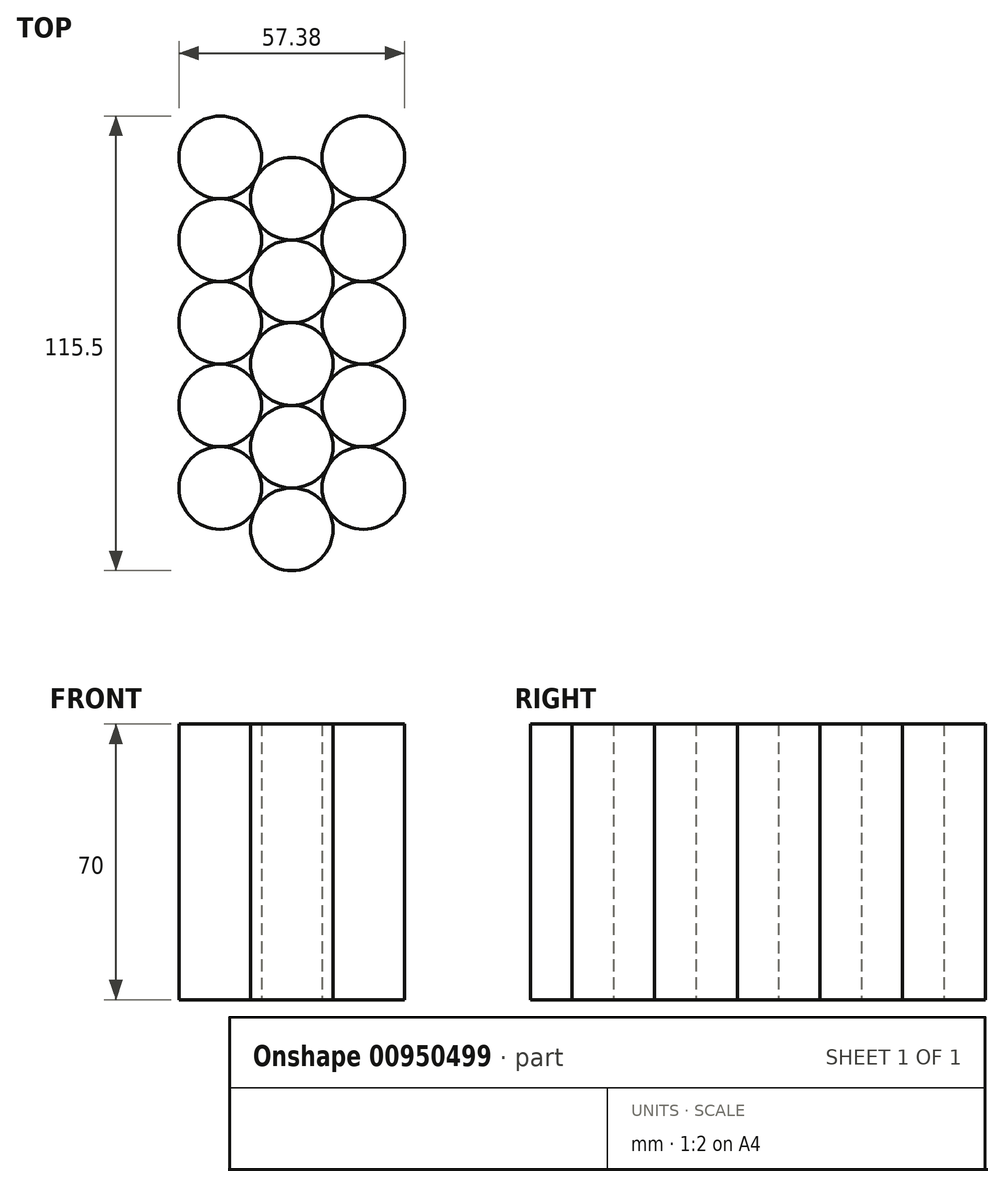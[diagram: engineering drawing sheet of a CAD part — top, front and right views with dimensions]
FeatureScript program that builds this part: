
annotation { "Feature Type Name" : "Feature", "Feature Type Description" : "" }
export const myFeature = defineFeature(function(context is Context, id is Id, definition is map)
    precondition{}
    {
        {
            var Q0;
            Q0=qCreatedBy(makeId("Top.planeOp"),FACE);
            var sketch = newSketch(context, id + "F0", { "sketchPlane" : qUnion([Q0])});
            skCircle(sketch, "E0", {"center": v(0, 0) * mm, "radius": 10.5 * mm});
            skCircle(sketch, "E1.0.1.0", {"center": v(0, 21) * mm, "radius": 10.5 * mm});
            skCircle(sketch, "E1.0.2.0", {"center": v(0, 42) * mm, "radius": 10.5 * mm});
            skCircle(sketch, "E1.0.3.0", {"center": v(0, 63) * mm, "radius": 10.5 * mm});
            skLineSegment(sketch, "E1.direction1", {"start": v(0, 0) * mm, "end": v(25, 0) * mm, "construction": true});
            skLineSegment(sketch, "E1.direction2", {"start": v(0, 0) * mm, "end": v(0, 21) * mm, "construction": true});
            skCircle(sketch, "E2", {"center": v(18.19, 10.5) * mm, "radius": 10.5 * mm});
            skCircle(sketch, "E3.0.1.0", {"center": v(18.19, 31.5) * mm, "radius": 10.5 * mm});
            skCircle(sketch, "E3.0.2.0", {"center": v(18.19, 52.5) * mm, "radius": 10.5 * mm});
            skCircle(sketch, "E3.0.3.0", {"center": v(18.19, 73.5) * mm, "radius": 10.5 * mm});
            skLineSegment(sketch, "E3.direction1", {"start": v(18.19, 10.5) * mm, "end": v(43.19, 10.5) * mm, "construction": true});
            skLineSegment(sketch, "E3.direction2", {"start": v(18.19, 10.5) * mm, "end": v(18.19, 31.5) * mm, "construction": true});
            skCircle(sketch, "E4", {"center": v(-18.19, 10.5) * mm, "radius": 10.5 * mm});
            skCircle(sketch, "E5.0.1.0", {"center": v(-18.19, 31.5) * mm, "radius": 10.5 * mm});
            skCircle(sketch, "E5.0.2.0", {"center": v(-18.19, 52.5) * mm, "radius": 10.5 * mm});
            skCircle(sketch, "E5.0.3.0", {"center": v(-18.19, 73.5) * mm, "radius": 10.5 * mm});
            skLineSegment(sketch, "E5.direction1", {"start": v(-18.19, 10.5) * mm, "end": v(9.41, 10.5) * mm, "construction": true});
            skLineSegment(sketch, "E5.direction2", {"start": v(-18.19, 10.5) * mm, "end": v(-18.19, 31.5) * mm, "construction": true});
            skLineSegment(sketch, "E6", {"start": v(0, -10.5) * mm, "end": v(0, 94.5) * mm, "construction": true});
            skCircle(sketch, "E7.0.0.4", {"center": v(0, 84) * mm, "radius": 10.5 * mm});
            skCircle(sketch, "E8", {"center": v(-18.19, 94.5) * mm, "radius": 10.5 * mm});
            skCircle(sketch, "E9", {"center": v(18.19, 94.5) * mm, "radius": 10.5 * mm});
            skSolve(sketch);
        }
        {
            var Q0;
            {var subQ0=sQuery(id+"F0.wireOp",EDGE,"E0");var subQ1=makeQuery(id+"F0.imprint","INTERSECT",VERTEX,{"derivedFrom":[subQ0,sQuery(id+"F0.wireOp",EDGE,"E1.0.1.0")]});Q0=makeQuery(id+"F0.imprint","IMPRINT",FACE,{"disambiguationData":[TD([[makeQuery(id+"F0.imprint","IMPRINT",EDGE,{"disambiguationData":[TD([[subQ1,1.0]])],"derivedFrom":subQ0}),1.0]])]});}
            var Q1;
            {var subQ0=sQuery(id+"F0.wireOp",EDGE,"E2");var subQ1=makeQuery(id+"F0.imprint","INTERSECT",VERTEX,{"derivedFrom":[subQ0,sQuery(id+"F0.wireOp",EDGE,"E3.0.1.0")]});Q1=makeQuery(id+"F0.imprint","IMPRINT",FACE,{"disambiguationData":[TD([[makeQuery(id+"F0.imprint","IMPRINT",EDGE,{"disambiguationData":[TD([[subQ1,-1.0]])],"derivedFrom":subQ0}),1.0]])]});}
            var Q2;
            {var subQ0=sQuery(id+"F0.wireOp",EDGE,"E1.0.1.0");var subQ1=makeQuery(id+"F0.imprint","INTERSECT",VERTEX,{"derivedFrom":[subQ0,sQuery(id+"F0.wireOp",EDGE,"E1.0.2.0")]});Q2=makeQuery(id+"F0.imprint","IMPRINT",FACE,{"disambiguationData":[TD([[makeQuery(id+"F0.imprint","IMPRINT",EDGE,{"disambiguationData":[TD([[subQ1,1.0]])],"derivedFrom":subQ0}),1.0]])]});}
            var Q3;
            {var subQ0=sQuery(id+"F0.wireOp",EDGE,"E3.0.1.0");var subQ1=makeQuery(id+"F0.imprint","INTERSECT",VERTEX,{"derivedFrom":[subQ0,sQuery(id+"F0.wireOp",EDGE,"E3.0.2.0")]});Q3=makeQuery(id+"F0.imprint","IMPRINT",FACE,{"disambiguationData":[TD([[makeQuery(id+"F0.imprint","IMPRINT",EDGE,{"disambiguationData":[TD([[subQ1,-1.0]])],"derivedFrom":subQ0}),1.0]])]});}
            var Q4;
            {var subQ0=sQuery(id+"F0.wireOp",EDGE,"E1.0.2.0");var subQ1=makeQuery(id+"F0.imprint","INTERSECT",VERTEX,{"derivedFrom":[subQ0,sQuery(id+"F0.wireOp",EDGE,"E1.0.3.0")]});Q4=makeQuery(id+"F0.imprint","IMPRINT",FACE,{"disambiguationData":[TD([[makeQuery(id+"F0.imprint","IMPRINT",EDGE,{"disambiguationData":[TD([[subQ1,1.0]])],"derivedFrom":subQ0}),1.0]])]});}
            var Q5;
            {var subQ0=sQuery(id+"F0.wireOp",EDGE,"E3.0.2.0");var subQ1=makeQuery(id+"F0.imprint","INTERSECT",VERTEX,{"derivedFrom":[subQ0,sQuery(id+"F0.wireOp",EDGE,"E3.0.3.0")]});Q5=makeQuery(id+"F0.imprint","IMPRINT",FACE,{"disambiguationData":[TD([[makeQuery(id+"F0.imprint","IMPRINT",EDGE,{"disambiguationData":[TD([[subQ1,-1.0]])],"derivedFrom":subQ0}),1.0]])]});}
            var Q6;
            {var subQ0=sQuery(id+"F0.wireOp",EDGE,"E1.0.3.0");var subQ1=makeQuery(id+"F0.imprint","INTERSECT",VERTEX,{"derivedFrom":[subQ0,sQuery(id+"F0.wireOp",EDGE,"E1.0.4.0")]});Q6=makeQuery(id+"F0.imprint","IMPRINT",FACE,{"disambiguationData":[TD([[makeQuery(id+"F0.imprint","IMPRINT",EDGE,{"disambiguationData":[TD([[subQ1,1.0]])],"derivedFrom":subQ0}),1.0]])]});}
            var Q7;
            {var subQ0=sQuery(id+"F0.wireOp",EDGE,"E3.0.3.0");var subQ1=makeQuery(id+"F0.imprint","INTERSECT",VERTEX,{"derivedFrom":[subQ0,sQuery(id+"F0.wireOp",EDGE,"E3.0.4.0")]});Q7=makeQuery(id+"F0.imprint","IMPRINT",FACE,{"disambiguationData":[TD([[makeQuery(id+"F0.imprint","IMPRINT",EDGE,{"disambiguationData":[TD([[subQ1,-1.0]])],"derivedFrom":subQ0}),1.0]])]});}
            var Q8;
            {var subQ0=sQuery(id+"F0.wireOp",EDGE,"E1.0.4.0");var subQ1=makeQuery(id+"F0.imprint","INTERSECT",VERTEX,{"derivedFrom":[subQ0,sQuery(id+"F0.wireOp",EDGE,"E1.0.5.0")]});Q8=makeQuery(id+"F0.imprint","IMPRINT",FACE,{"disambiguationData":[TD([[makeQuery(id+"F0.imprint","IMPRINT",EDGE,{"disambiguationData":[TD([[subQ1,1.0]])],"derivedFrom":subQ0}),1.0]])]});}
            var Q9;
            {var subQ0=sQuery(id+"F0.wireOp",EDGE,"E3.0.4.0");var subQ1=makeQuery(id+"F0.imprint","INTERSECT",VERTEX,{"derivedFrom":[subQ0,sQuery(id+"F0.wireOp",EDGE,"E3.0.5.0")]});Q9=makeQuery(id+"F0.imprint","IMPRINT",FACE,{"disambiguationData":[TD([[makeQuery(id+"F0.imprint","IMPRINT",EDGE,{"disambiguationData":[TD([[subQ1,-1.0]])],"derivedFrom":subQ0}),1.0]])]});}
            var Q10;
            {var subQ0=sQuery(id+"F0.wireOp",EDGE,"E1.0.5.0");var subQ1=makeQuery(id+"F0.imprint","INTERSECT",VERTEX,{"derivedFrom":[subQ0,sQuery(id+"F0.wireOp",EDGE,"E1.0.6.0")]});Q10=makeQuery(id+"F0.imprint","IMPRINT",FACE,{"disambiguationData":[TD([[makeQuery(id+"F0.imprint","IMPRINT",EDGE,{"disambiguationData":[TD([[subQ1,1.0]])],"derivedFrom":subQ0}),1.0]])]});}
            var Q11;
            {var subQ0=sQuery(id+"F0.wireOp",EDGE,"E3.0.5.0");var subQ1=makeQuery(id+"F0.imprint","INTERSECT",VERTEX,{"derivedFrom":[subQ0,sQuery(id+"F0.wireOp",EDGE,"E3.0.6.0")]});Q11=makeQuery(id+"F0.imprint","IMPRINT",FACE,{"disambiguationData":[TD([[makeQuery(id+"F0.imprint","IMPRINT",EDGE,{"disambiguationData":[TD([[subQ1,-1.0]])],"derivedFrom":subQ0}),1.0]])]});}
            var Q12;
            {var subQ0=sQuery(id+"F0.wireOp",EDGE,"E1.0.6.0");var subQ1=makeQuery(id+"F0.imprint","INTERSECT",VERTEX,{"derivedFrom":[subQ0,sQuery(id+"F0.wireOp",EDGE,"E1.0.7.0")]});Q12=makeQuery(id+"F0.imprint","IMPRINT",FACE,{"disambiguationData":[TD([[makeQuery(id+"F0.imprint","IMPRINT",EDGE,{"disambiguationData":[TD([[subQ1,1.0]])],"derivedFrom":subQ0}),1.0]])]});}
            var Q13;
            {var subQ0=sQuery(id+"F0.wireOp",EDGE,"E3.0.6.0");var subQ1=makeQuery(id+"F0.imprint","INTERSECT",VERTEX,{"derivedFrom":[subQ0,sQuery(id+"F0.wireOp",EDGE,"E3.0.7.0")]});Q13=makeQuery(id+"F0.imprint","IMPRINT",FACE,{"disambiguationData":[TD([[makeQuery(id+"F0.imprint","IMPRINT",EDGE,{"disambiguationData":[TD([[subQ1,-1.0]])],"derivedFrom":subQ0}),1.0]])]});}
            var Q14;
            {var subQ0=sQuery(id+"F0.wireOp",EDGE,"E1.0.7.0");var subQ1=makeQuery(id+"F0.imprint","INTERSECT",VERTEX,{"derivedFrom":[subQ0,sQuery(id+"F0.wireOp",EDGE,"E1.0.8.0")]});Q14=makeQuery(id+"F0.imprint","IMPRINT",FACE,{"disambiguationData":[TD([[makeQuery(id+"F0.imprint","IMPRINT",EDGE,{"disambiguationData":[TD([[subQ1,1.0]])],"derivedFrom":subQ0}),1.0]])]});}
            var Q15;
            {var subQ0=sQuery(id+"F0.wireOp",EDGE,"E3.0.7.0");var subQ1=makeQuery(id+"F0.imprint","INTERSECT",VERTEX,{"derivedFrom":[subQ0,sQuery(id+"F0.wireOp",EDGE,"E3.0.8.0")]});Q15=makeQuery(id+"F0.imprint","IMPRINT",FACE,{"disambiguationData":[TD([[makeQuery(id+"F0.imprint","IMPRINT",EDGE,{"disambiguationData":[TD([[subQ1,-1.0]])],"derivedFrom":subQ0}),1.0]])]});}
            var Q16;
            {var subQ0=sQuery(id+"F0.wireOp",EDGE,"E1.0.8.0");var subQ1=makeQuery(id+"F0.imprint","INTERSECT",VERTEX,{"derivedFrom":[subQ0,sQuery(id+"F0.wireOp",EDGE,"E1.0.9.0")]});Q16=makeQuery(id+"F0.imprint","IMPRINT",FACE,{"disambiguationData":[TD([[makeQuery(id+"F0.imprint","IMPRINT",EDGE,{"disambiguationData":[TD([[subQ1,1.0]])],"derivedFrom":subQ0}),1.0]])]});}
            var Q17;
            {var subQ0=sQuery(id+"F0.wireOp",EDGE,"E3.0.8.0");var subQ1=makeQuery(id+"F0.imprint","INTERSECT",VERTEX,{"derivedFrom":[subQ0,sQuery(id+"F0.wireOp",EDGE,"E3.0.9.0")]});Q17=makeQuery(id+"F0.imprint","IMPRINT",FACE,{"disambiguationData":[TD([[makeQuery(id+"F0.imprint","IMPRINT",EDGE,{"disambiguationData":[TD([[subQ1,-1.0]])],"derivedFrom":subQ0}),1.0]])]});}
            var Q18;
            {var subQ0=sQuery(id+"F0.wireOp",EDGE,"E1.0.9.0");var subQ1=makeQuery(id+"F0.imprint","INTERSECT",VERTEX,{"derivedFrom":[subQ0,sQuery(id+"F0.wireOp",EDGE,"E1.0.10.0")]});Q18=makeQuery(id+"F0.imprint","IMPRINT",FACE,{"disambiguationData":[TD([[makeQuery(id+"F0.imprint","IMPRINT",EDGE,{"disambiguationData":[TD([[subQ1,1.0]])],"derivedFrom":subQ0}),1.0]])]});}
            var Q19;
            {var subQ0=sQuery(id+"F0.wireOp",EDGE,"E3.0.9.0");var subQ1=makeQuery(id+"F0.imprint","INTERSECT",VERTEX,{"derivedFrom":[subQ0,sQuery(id+"F0.wireOp",EDGE,"E3.0.10.0")]});Q19=makeQuery(id+"F0.imprint","IMPRINT",FACE,{"disambiguationData":[TD([[makeQuery(id+"F0.imprint","IMPRINT",EDGE,{"disambiguationData":[TD([[subQ1,-1.0]])],"derivedFrom":subQ0}),1.0]])]});}
            var Q20;
            {var subQ0=sQuery(id+"F0.wireOp",EDGE,"E1.0.10.0");var subQ1=makeQuery(id+"F0.imprint","INTERSECT",VERTEX,{"derivedFrom":[subQ0,sQuery(id+"F0.wireOp",EDGE,"E1.0.11.0")]});Q20=makeQuery(id+"F0.imprint","IMPRINT",FACE,{"disambiguationData":[TD([[makeQuery(id+"F0.imprint","IMPRINT",EDGE,{"disambiguationData":[TD([[subQ1,1.0]])],"derivedFrom":subQ0}),1.0]])]});}
            var Q21;
            {var subQ0=sQuery(id+"F0.wireOp",EDGE,"E3.0.10.0");var subQ1=makeQuery(id+"F0.imprint","INTERSECT",VERTEX,{"derivedFrom":[subQ0,sQuery(id+"F0.wireOp",EDGE,"E3.0.11.0")]});Q21=makeQuery(id+"F0.imprint","IMPRINT",FACE,{"disambiguationData":[TD([[makeQuery(id+"F0.imprint","IMPRINT",EDGE,{"disambiguationData":[TD([[subQ1,-1.0]])],"derivedFrom":subQ0}),1.0]])]});}
            var Q22;
            {var subQ0=sQuery(id+"F0.wireOp",EDGE,"E1.0.11.0");var subQ1=makeQuery(id+"F0.imprint","INTERSECT",VERTEX,{"derivedFrom":[subQ0,sQuery(id+"F0.wireOp",EDGE,"E1.0.12.0")]});Q22=makeQuery(id+"F0.imprint","IMPRINT",FACE,{"disambiguationData":[TD([[makeQuery(id+"F0.imprint","IMPRINT",EDGE,{"disambiguationData":[TD([[subQ1,1.0]])],"derivedFrom":subQ0}),1.0]])]});}
            var Q23;
            {var subQ0=sQuery(id+"F0.wireOp",EDGE,"E3.0.11.0");var subQ1=makeQuery(id+"F0.imprint","INTERSECT",VERTEX,{"derivedFrom":[subQ0,sQuery(id+"F0.wireOp",EDGE,"E3.0.12.0")]});Q23=makeQuery(id+"F0.imprint","IMPRINT",FACE,{"disambiguationData":[TD([[makeQuery(id+"F0.imprint","IMPRINT",EDGE,{"disambiguationData":[TD([[subQ1,-1.0]])],"derivedFrom":subQ0}),1.0]])]});}
            var Q24;
            {var subQ0=sQuery(id+"F0.wireOp",EDGE,"E1.0.12.0");var subQ1=makeQuery(id+"F0.imprint","INTERSECT",VERTEX,{"derivedFrom":[subQ0,sQuery(id+"F0.wireOp",EDGE,"E1.0.13.0")]});Q24=makeQuery(id+"F0.imprint","IMPRINT",FACE,{"disambiguationData":[TD([[makeQuery(id+"F0.imprint","IMPRINT",EDGE,{"disambiguationData":[TD([[subQ1,1.0]])],"derivedFrom":subQ0}),1.0]])]});}
            var Q25;
            {var subQ0=sQuery(id+"F0.wireOp",EDGE,"E3.0.12.0");var subQ1=makeQuery(id+"F0.imprint","INTERSECT",VERTEX,{"derivedFrom":[subQ0,sQuery(id+"F0.wireOp",EDGE,"E3.0.13.0")]});Q25=makeQuery(id+"F0.imprint","IMPRINT",FACE,{"disambiguationData":[TD([[makeQuery(id+"F0.imprint","IMPRINT",EDGE,{"disambiguationData":[TD([[subQ1,-1.0]])],"derivedFrom":subQ0}),1.0]])]});}
            var Q26;
            {var subQ0=sQuery(id+"F0.wireOp",EDGE,"E1.0.13.0");var subQ1=makeQuery(id+"F0.imprint","INTERSECT",VERTEX,{"derivedFrom":[sQuery(id+"F0.wireOp",EDGE,"E1.0.12.0"),subQ0]});Q26=makeQuery(id+"F0.imprint","IMPRINT",FACE,{"disambiguationData":[TD([[makeQuery(id+"F0.imprint","IMPRINT",EDGE,{"disambiguationData":[TD([[subQ1,1.0]])],"derivedFrom":subQ0}),1.0]])]});}
            var Q27;
            {var subQ0=sQuery(id+"F0.wireOp",EDGE,"E3.0.13.0");var subQ1=makeQuery(id+"F0.imprint","INTERSECT",VERTEX,{"derivedFrom":[sQuery(id+"F0.wireOp",EDGE,"E1.0.13.0"),subQ0]});Q27=makeQuery(id+"F0.imprint","IMPRINT",FACE,{"disambiguationData":[TD([[makeQuery(id+"F0.imprint","IMPRINT",EDGE,{"disambiguationData":[TD([[subQ1,-1.0]])],"derivedFrom":subQ0}),1.0]])]});}
            var Q28;
            {var subQ0=sQuery(id+"F0.wireOp",EDGE,"E7.0.0.4");var subQ1=makeQuery(id+"F0.imprint","INTERSECT",VERTEX,{"derivedFrom":[sQuery(id+"F0.wireOp",EDGE,"E5.0.3.0"),subQ0]});Q28=makeQuery(id+"F0.imprint","IMPRINT",FACE,{"disambiguationData":[TD([[makeQuery(id+"F0.imprint","IMPRINT",EDGE,{"disambiguationData":[TD([[subQ1,-1.0]])],"derivedFrom":subQ0}),1.0]])]});}
            var Q29;
            {var subQ0=sQuery(id+"F0.wireOp",EDGE,"E5.0.3.0");var subQ1=makeQuery(id+"F0.imprint","INTERSECT",VERTEX,{"derivedFrom":[sQuery(id+"F0.wireOp",EDGE,"E5.0.2.0"),subQ0]});Q29=makeQuery(id+"F0.imprint","IMPRINT",FACE,{"disambiguationData":[TD([[makeQuery(id+"F0.imprint","IMPRINT",EDGE,{"disambiguationData":[TD([[subQ1,1.0]])],"derivedFrom":subQ0}),1.0]])]});}
            var Q30;
            {var subQ0=sQuery(id+"F0.wireOp",EDGE,"E5.0.2.0");var subQ1=makeQuery(id+"F0.imprint","INTERSECT",VERTEX,{"derivedFrom":[subQ0,sQuery(id+"F0.wireOp",EDGE,"E5.0.3.0")]});Q30=makeQuery(id+"F0.imprint","IMPRINT",FACE,{"disambiguationData":[TD([[makeQuery(id+"F0.imprint","IMPRINT",EDGE,{"disambiguationData":[TD([[subQ1,1.0]])],"derivedFrom":subQ0}),1.0]])]});}
            var Q31;
            {var subQ0=sQuery(id+"F0.wireOp",EDGE,"E5.0.1.0");var subQ1=makeQuery(id+"F0.imprint","INTERSECT",VERTEX,{"derivedFrom":[subQ0,sQuery(id+"F0.wireOp",EDGE,"E5.0.2.0")]});Q31=makeQuery(id+"F0.imprint","IMPRINT",FACE,{"disambiguationData":[TD([[makeQuery(id+"F0.imprint","IMPRINT",EDGE,{"disambiguationData":[TD([[subQ1,1.0]])],"derivedFrom":subQ0}),1.0]])]});}
            var Q32;
            {var subQ0=sQuery(id+"F0.wireOp",EDGE,"E4");var subQ1=makeQuery(id+"F0.imprint","INTERSECT",VERTEX,{"derivedFrom":[subQ0,sQuery(id+"F0.wireOp",EDGE,"E5.0.1.0")]});Q32=makeQuery(id+"F0.imprint","IMPRINT",FACE,{"disambiguationData":[TD([[makeQuery(id+"F0.imprint","IMPRINT",EDGE,{"disambiguationData":[TD([[subQ1,1.0]])],"derivedFrom":subQ0}),1.0]])]});}
            var Q33;
            {var subQ0=sQuery(id+"F0.wireOp",EDGE,"E9");var subQ1=makeQuery(id+"F0.imprint","INTERSECT",VERTEX,{"derivedFrom":[sQuery(id+"F0.wireOp",EDGE,"E3.0.3.0"),subQ0]});Q33=makeQuery(id+"F0.imprint","IMPRINT",FACE,{"disambiguationData":[TD([[makeQuery(id+"F0.imprint","IMPRINT",EDGE,{"disambiguationData":[TD([[subQ1,1.0]])],"derivedFrom":subQ0}),1.0]])]});}
            var Q34;
            {var subQ0=sQuery(id+"F0.wireOp",EDGE,"E8");var subQ1=makeQuery(id+"F0.imprint","INTERSECT",VERTEX,{"derivedFrom":[sQuery(id+"F0.wireOp",EDGE,"E5.0.3.0"),subQ0]});Q34=makeQuery(id+"F0.imprint","IMPRINT",FACE,{"disambiguationData":[TD([[makeQuery(id+"F0.imprint","IMPRINT",EDGE,{"disambiguationData":[TD([[subQ1,-1.0]])],"derivedFrom":subQ0}),1.0]])]});}
            extrude(context, id + "F1", {"entities" : qUnion([Q0, Q1, Q2, Q3, Q4, Q5, Q6, Q7, Q8, Q9, Q10, Q11, Q12, Q13, Q14, Q15, Q16, Q17, Q18, Q19, Q20, Q21, Q22, Q23, Q24, Q25, Q26, Q27, Q28, Q29, Q30, Q31, Q32, Q33, Q34]), "depth" : 70 * mm, "offsetDistance" : 25 * mm});
        }
    });
